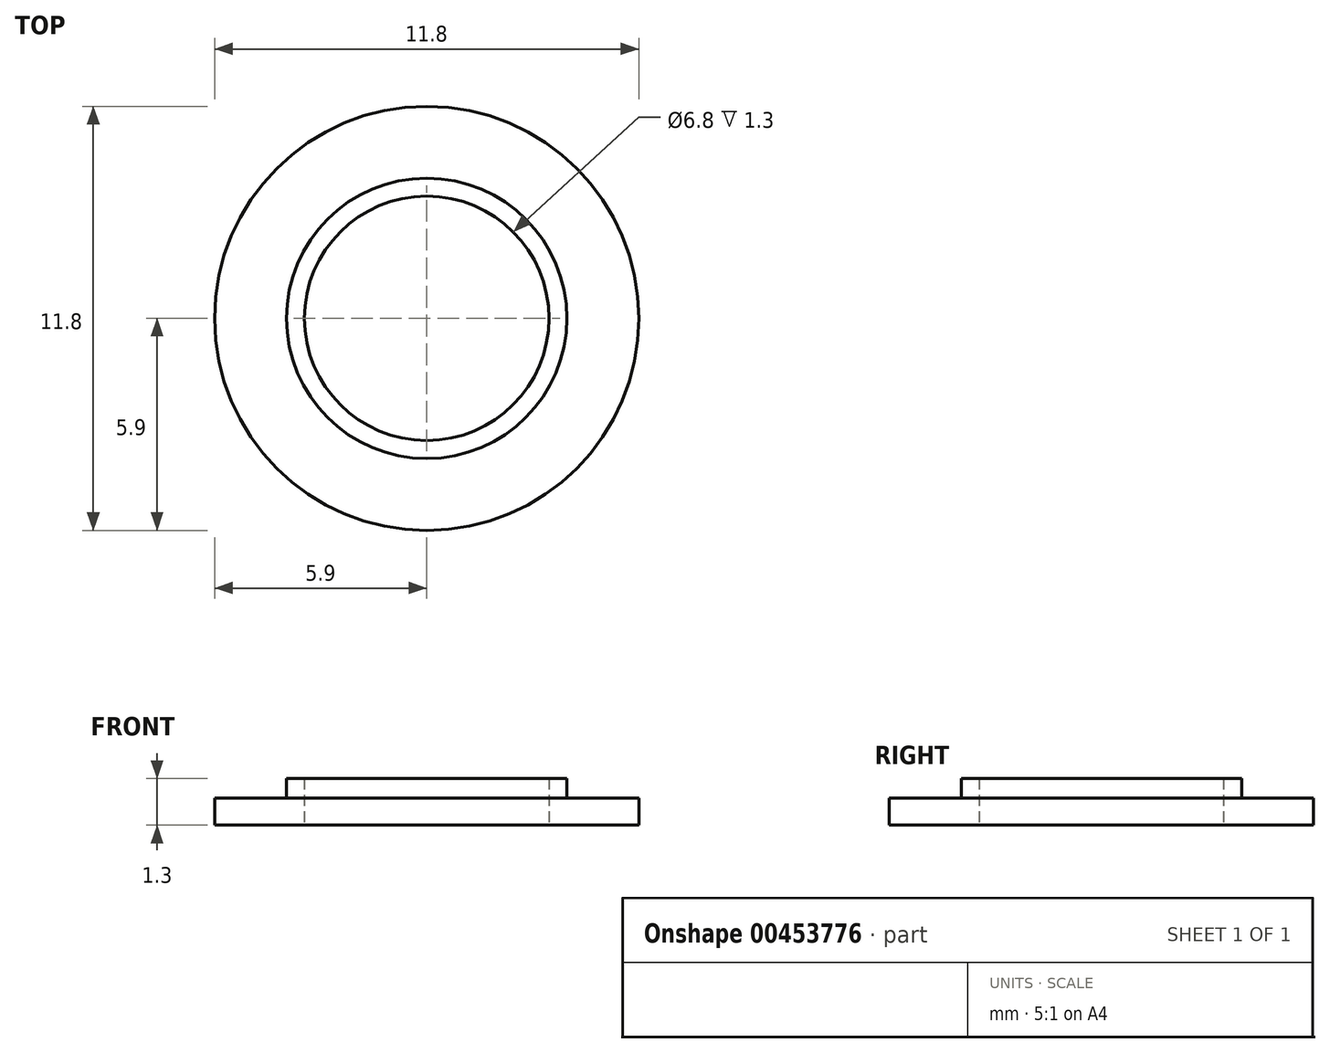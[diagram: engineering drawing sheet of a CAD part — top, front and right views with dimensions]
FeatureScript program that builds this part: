
annotation { "Feature Type Name" : "Feature", "Feature Type Description" : "" }
export const myFeature = defineFeature(function(context is Context, id is Id, definition is map)
    precondition{}
    {
        {
            var Q0;
            Q0=qCreatedBy(makeId("Top.planeOp"),FACE);
            var sketch = newSketch(context, id + "F0", { "sketchPlane" : qUnion([Q0])});
            skCircle(sketch, "E0", {"center": v(0, 0) * mm, "radius": 3.4 * mm});
            skCircle(sketch, "E1.0", {"center": v(0, 0) * mm, "radius": 3.9 * mm});
            skCircle(sketch, "E2.0", {"center": v(0, 0) * mm, "radius": 5.9 * mm});
            skSolve(sketch);
        }
        {
            var Q0;
            Q0=makeQuery(id+"F0.imprint","IMPRINT",FACE,{"disambiguationData":[TD([[makeQuery(id+"F0.imprint","IMPRINT",EDGE,{"derivedFrom":sQuery(id+"F0.wireOp",EDGE,"E1.0")}),-1.0]])]});
            extrude(context, id + "F1", {"entities" : qUnion([Q0]), "depth" : .75 * mm});
        }
        {
            var Q0;
            Q0=makeQuery(id+"F0.imprint","IMPRINT",FACE,{"disambiguationData":[TD([[makeQuery(id+"F0.imprint","IMPRINT",EDGE,{"derivedFrom":sQuery(id+"F0.wireOp",EDGE,"E0")}),-1.0]])]});
            extrude(context, id + "F2", {"entities" : qUnion([Q0]), "operationType" : NewBodyOperationType.ADD, "depth" : 1.3 * mm});
        }
    });
